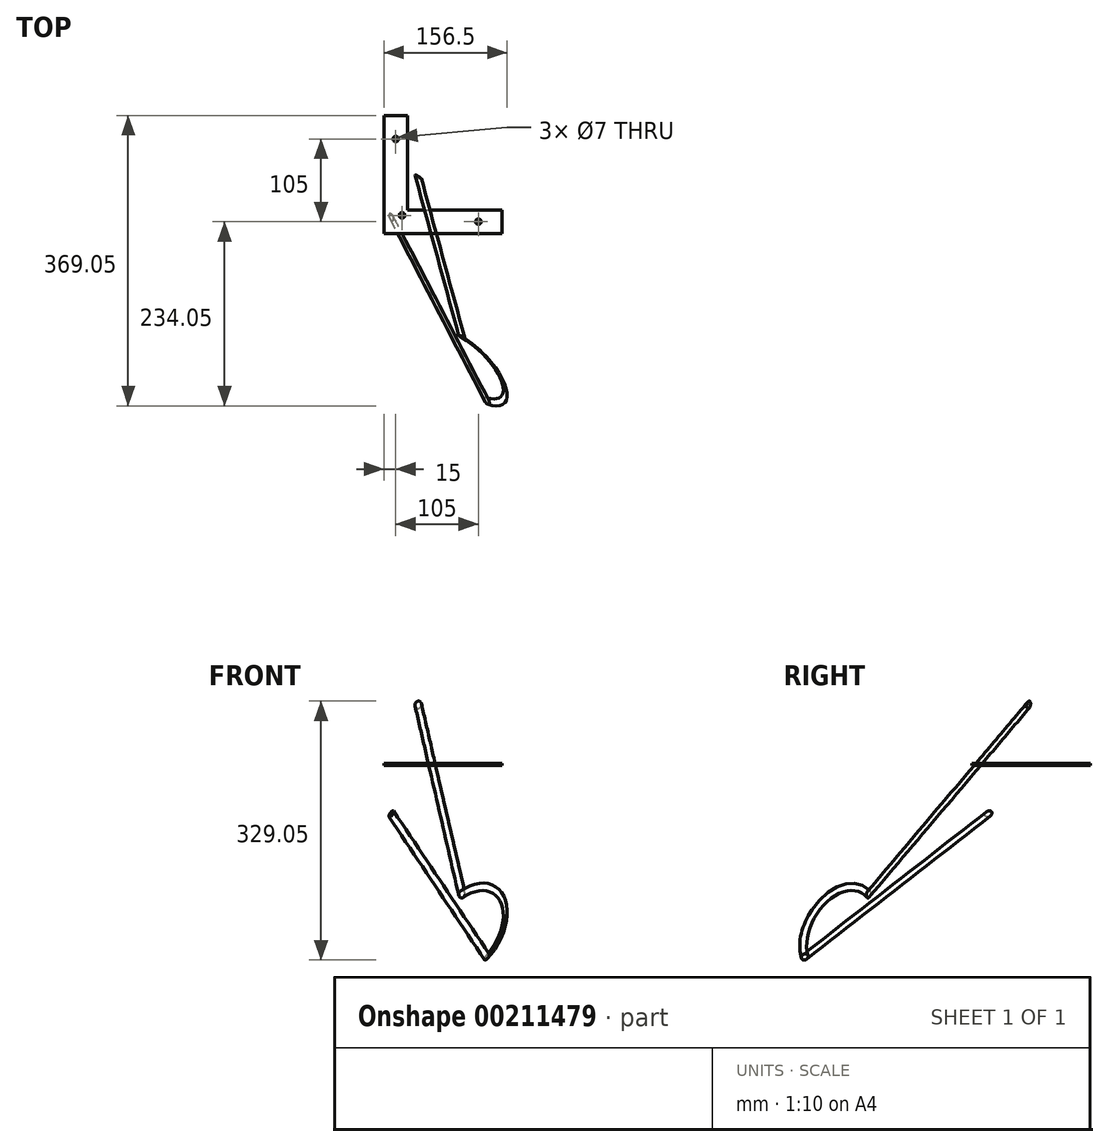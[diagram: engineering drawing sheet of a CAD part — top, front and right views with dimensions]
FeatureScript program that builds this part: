
annotation { "Feature Type Name" : "Feature", "Feature Type Description" : "" }
export const myFeature = defineFeature(function(context is Context, id is Id, definition is map)
    precondition{}
    {
        {
            var Q0;
            Q0=qCreatedBy(makeId("Top.planeOp"),FACE);
            var sketch = newSketch(context, id + "F0", { "sketchPlane" : qUnion([Q0])});
            skLineSegment(sketch, "E0", {"start": v(0, 0) * mm, "end": v(0, 150) * mm});
            skLineSegment(sketch, "E1", {"start": v(0, 150) * mm, "end": v(30, 150) * mm});
            skLineSegment(sketch, "E2", {"start": v(30, 150) * mm, "end": v(30, 30) * mm});
            skLineSegment(sketch, "E3", {"start": v(30, 30) * mm, "end": v(150, 30) * mm});
            skLineSegment(sketch, "E4", {"start": v(150, 30) * mm, "end": v(150, 0) * mm});
            skLineSegment(sketch, "E5", {"start": v(150, 0) * mm, "end": v(0, 0) * mm});
            skLineSegment(sketch, "E6", {"start": v(0, 150) * mm, "end": v(10, 150) * mm});
            skLineSegment(sketch, "E7", {"start": v(10, 150) * mm, "end": v(10, -10.8) * mm, "construction": true});
            skLineSegment(sketch, "E8", {"start": v(150, 0) * mm, "end": v(150, 10) * mm});
            skLineSegment(sketch, "E9", {"start": v(150, 10) * mm, "end": v(-41.67, 10) * mm, "construction": true});
            skCircle(sketch, "E10", {"center": v(10, 10) * mm, "radius": 4.75 * mm});
            skLineSegment(sketch, "E11", {"start": v(150, 10) * mm, "end": v(90, 10) * mm, "construction": true});
            skLineSegment(sketch, "E12", {"start": v(10, 150) * mm, "end": v(10, 90) * mm, "construction": true});
            skCircle(sketch, "E13", {"center": v(10, 90) * mm, "radius": 4.75 * mm});
            skCircle(sketch, "E14", {"center": v(90, 10) * mm, "radius": 4.75 * mm});
            skLineSegment(sketch, "E15", {"start": v(15, 150) * mm, "end": v(15, 120) * mm, "construction": true});
            skLineSegment(sketch, "E16", {"start": v(150, 15) * mm, "end": v(120, 15) * mm, "construction": true});
            skLineSegment(sketch, "E17", {"start": v(30, 30) * mm, "end": v(30, 23) * mm, "construction": true});
            skLineSegment(sketch, "E18", {"start": v(30, 23) * mm, "end": v(23, 23) * mm, "construction": true});
            skCircle(sketch, "E19", {"center": v(23, 23) * mm, "radius": 3.5 * mm});
            skCircle(sketch, "E20", {"center": v(120, 15) * mm, "radius": 3.5 * mm});
            skCircle(sketch, "E21", {"center": v(15, 120) * mm, "radius": 3.5 * mm});
            skLineSegment(sketch, "E22", {"start": v(10, 90) * mm, "end": v(90, 10) * mm, "construction": true});
            skLineSegment(sketch, "E23", {"start": v(10, 10) * mm, "end": v(87.96, -67.96) * mm, "construction": true});
            skSolve(sketch);
        }
        {
            var Q0;
            Q0=qSketchRegion(id+"F0",true);
            var Q1;
            Q1=makeQuery(id+"F0.imprint","IMPRINT",FACE,{"disambiguationData":[TD([[makeQuery(id+"F0.imprint","IMPRINT",EDGE,{"derivedFrom":sQuery(id+"F0.wireOp",EDGE,"E10")}),1.0]])]});
            var Q2;
            Q2=makeQuery(id+"F0.imprint","IMPRINT",FACE,{"disambiguationData":[TD([[makeQuery(id+"F0.imprint","IMPRINT",EDGE,{"derivedFrom":sQuery(id+"F0.wireOp",EDGE,"E14")}),1.0]])]});
            var Q3;
            Q3=makeQuery(id+"F0.imprint","IMPRINT",FACE,{"disambiguationData":[TD([[makeQuery(id+"F0.imprint","IMPRINT",EDGE,{"derivedFrom":sQuery(id+"F0.wireOp",EDGE,"E13")}),1.0]])]});
            extrude(context, id + "F1", {"entities" : qUnion([Q0, Q1, Q2, Q3]), "depth" : 2.5 * mm});
        }
        {
            var Q0;
            Q0=qCreatedBy(makeId("Right.planeOp"),FACE);
            var sketch = newSketch(context, id + "F2", { "sketchPlane" : qUnion([Q0])});
            skLineSegment(sketch, "E24", {"start": v(0, 0) * mm, "end": v(0, -325) * mm});
            skLineSegment(sketch, "E25", {"start": v(0, -325) * mm, "end": v(-50, -325) * mm});
            skSolve(sketch);
        }
        {
            var Q0;
            Q0=qCreatedBy(makeId("Front.planeOp"),FACE);
            var sketch = newSketch(context, id + "F3", { "sketchPlane" : qUnion([Q0])});
            skLineSegment(sketch, "E26", {"start": v(0, 0) * mm, "end": v(0, -325) * mm});
            skLineSegment(sketch, "E27", {"start": v(0, -325) * mm, "end": v(-50, -325) * mm});
            skSolve(sketch);
        }
        {
            var Q0;
            Q0=sQuery(id+"F3.wireOp",VERTEX,"E27.end");
            var Q1;
            Q1=sQuery(id+"F3.wireOp",VERTEX,"E27.start");
            var Q2;
            Q2=sQuery(id+"F2.wireOp",VERTEX,"E25.end");
            cPlane(context, id + "F4", {"entities" : qUnion([Q0, Q1, Q2]), "cplaneType" : CPlaneType.THREE_POINT, "offset" : 150 * mm, "width" : 150 * mm, "height" : 150 * mm});
        }
        {
            var Q0;
            Q0=qCreatedBy(id+"F4.planeOp",FACE);
            var sketch = newSketch(context, id + "F5", { "sketchPlane" : qUnion([Q0])});
            skLineSegment(sketch, "E28.bottom", {"start": v(0, 0) * mm, "end": v(-50, 0) * mm});
            skLineSegment(sketch, "E28.top", {"start": v(0, -50) * mm, "end": v(-50, -50) * mm});
            skLineSegment(sketch, "E28.left", {"start": v(0, 0) * mm, "end": v(0, -50) * mm});
            skLineSegment(sketch, "E28.right", {"start": v(-50, 0) * mm, "end": v(-50, -50) * mm});
            skSolve(sketch);
        }
        {
            var Q0;
            Q0=sQuery(id+"F0.wireOp",VERTEX,"E13.center");
            var Q1;
            Q1=sQuery(id+"F0.wireOp",VERTEX,"E14.center");
            var Q2;
            Q2=sQuery(id+"F5.wireOp",VERTEX,"E28.right.end");
            cPlane(context, id + "F6", {"entities" : qUnion([Q0, Q1, Q2]), "cplaneType" : CPlaneType.THREE_POINT, "offset" : 150 * mm, "width" : 150 * mm, "height" : 150 * mm});
        }
        {
            var Q0;
            Q0=qCreatedBy(id+"F6.planeOp",FACE);
            var sketch = newSketch(context, id + "F7", { "sketchPlane" : qUnion([Q0])});
            skPoint(sketch, "E29", {"position": v(-63, 5.24) * mm});
            skPoint(sketch, "E30", {"position": v(42.08, 47.17) * mm});
            skPoint(sketch, "E31", {"position": v(120.9, -303) * mm});
            skLineSegment(sketch, "E32", {"start": v(120.9, -303) * mm, "end": v(-63, 5.24) * mm, "construction": true});
            skLineSegment(sketch, "E33", {"start": v(42.08, 47.17) * mm, "end": v(120.9, -303) * mm, "construction": true});
            skLineSegment(sketch, "E34", {"start": v(-63, 5.24) * mm, "end": v(42.08, 47.17) * mm, "construction": true});
            skLineSegment(sketch, "E35", {"start": v(114.95, -264.51) * mm, "end": v(42.08, 47.17) * mm});
            skLineSegment(sketch, "E36", {"start": v(-63, 5.24) * mm, "end": v(96.54, -271.78) * mm});
            skPoint(sketch, "E37.visualSharp", {"position": v(130.38, -330.54) * mm});
            skArc(sketch, "E37.filletArc", {"start": v(96.54, -271.78) * mm, "mid": v(108.88, -276.1) * mm, "end": v(114.95, -264.51) * mm});
            skLineSegment(sketch, "E38", {"start": v(108.88, -276.1) * mm, "end": v(-10.46, 26.2) * mm});
            skSolve(sketch);
        }
        {
            var Q0;
            Q0=sQuery(id+"F7.wireOp",EDGE,"E34");
            cPlane(context, id + "F8", {"entities" : qUnion([Q0]), "cplaneType" : CPlaneType.LINE_ANGLE, "offset" : 150 * mm, "angle" : 168 * degree, "width" : 150 * mm, "height" : 150 * mm});
        }
        {
            var Q0;
            Q0=qCreatedBy(id+"F8.planeOp",FACE);
            var sketch = newSketch(context, id + "F9", { "sketchPlane" : qUnion([Q0])});
            skPoint(sketch, "E39", {"position": v(7.92, 89) * mm});
            skPoint(sketch, "E40", {"position": v(88.8, 9.89) * mm});
            skCircle(sketch, "E41", {"center": v(7.92, 89) * mm, "radius": 4.75 * mm});
            skSolve(sketch);
        }
        {
            var Q0;
            Q0=qSketchRegion(id+"F9",true);
            var Q1;
            Q1=sQuery(id+"F9.wireOp",EDGE,"E41");
            var Q2;
            Q2=sQuery(id+"F7.wireOp",EDGE,"E36");
            var Q3;
            Q3=sQuery(id+"F7.wireOp",EDGE,"E37.filletArc");
            var Q4;
            Q4=sQuery(id+"F7.wireOp",EDGE,"E35");
            sweep(context, id + "F10", {"profiles" : qUnion([Q0]), "surfaceProfiles" : qUnion([Q1]), "path" : qUnion([Q2, Q3, Q4])});
        }
        {
            var Q0;
            Q0=sQuery(id+"F0.wireOp",VERTEX,"E23.start");
            var Q1;
            Q1=sQuery(id+"F0.wireOp",VERTEX,"E23.end");
            var Q2;
            Q2=sQuery(id+"F5.wireOp",VERTEX,"E28.right.end");
            cPlane(context, id + "F11", {"entities" : qUnion([Q0, Q1, Q2]), "cplaneType" : CPlaneType.THREE_POINT, "offset" : 150 * mm, "width" : 150 * mm, "height" : 150 * mm});
        }
        {
            var Q0;
            Q0=qCreatedBy(id+"F11.planeOp",FACE);
            var sketch = newSketch(context, id + "F12", { "sketchPlane" : qUnion([Q0])});
            skPoint(sketch, "E42", {"position": v(81.4, -322.2) * mm});
            skPoint(sketch, "E43", {"position": v(-0.88, 3.46) * mm});
            skLineSegment(sketch, "E44", {"start": v(-0.88, 3.46) * mm, "end": v(81.4, -322.2) * mm, "construction": true});
            skLineSegment(sketch, "E45", {"start": v(121.51, -481.02) * mm, "end": v(129.75, -513.61) * mm, "construction": true});
            skLineSegment(sketch, "E46", {"start": v(129.75, -513.61) * mm, "end": v(-0.88, 3.46) * mm});
            skSolve(sketch);
        }
        {
            var Q0;
            Q0=qCreatedBy(id+"F8.planeOp",FACE);
            var Q1;
            Q1=sQuery(id+"F12.wireOp",VERTEX,"E43");
            cPlane(context, id + "F13", {"entities" : qUnion([Q0, Q1]), "cplaneType" : CPlaneType.PLANE_POINT, "offset" : 150 * mm, "width" : 150 * mm, "height" : 150 * mm});
        }
    });
